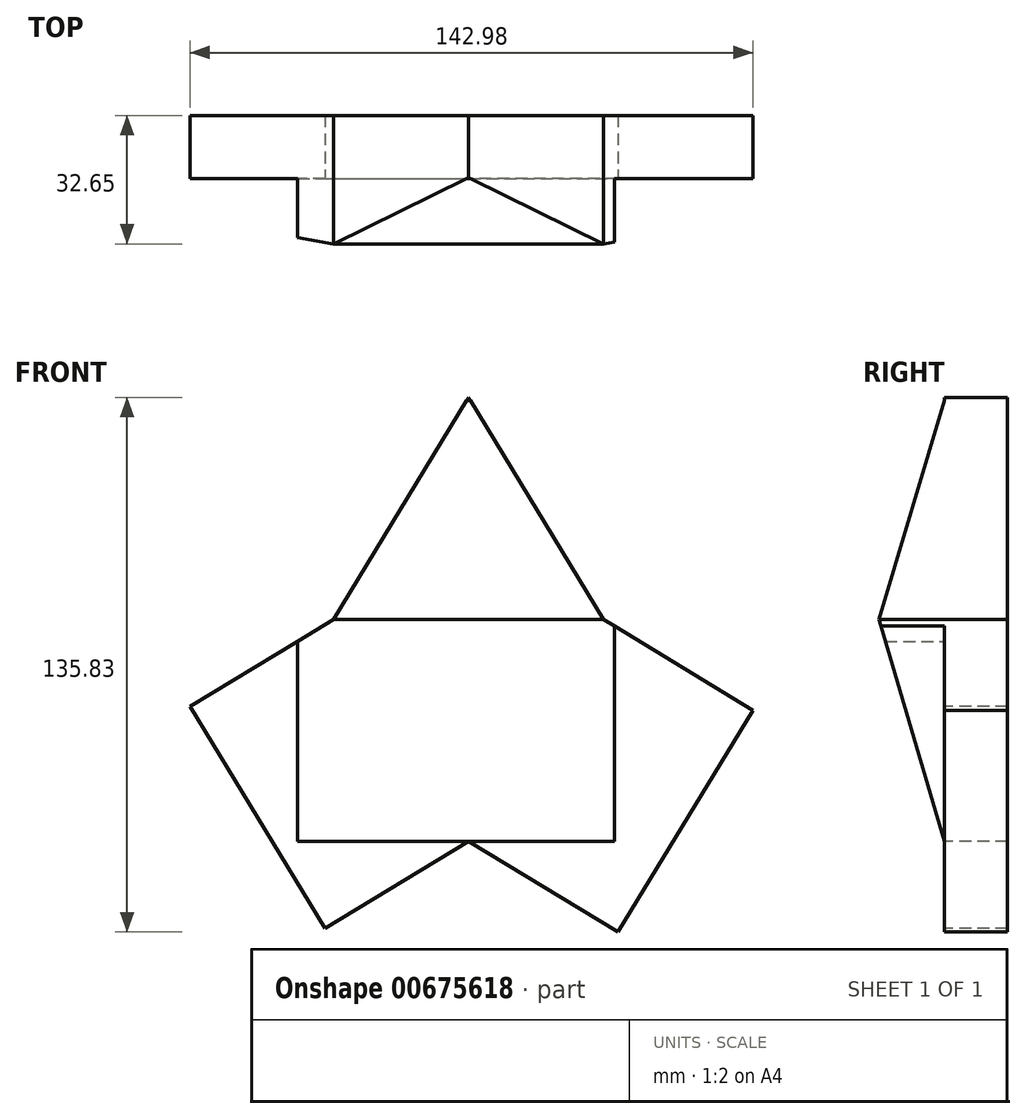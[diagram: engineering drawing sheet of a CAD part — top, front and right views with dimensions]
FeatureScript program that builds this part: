
annotation { "Feature Type Name" : "Feature", "Feature Type Description" : "" }
export const myFeature = defineFeature(function(context is Context, id is Id, definition is map)
    precondition{}
    {
        {
            var Q0;
            Q0=qCreatedBy(makeId("Front.planeOp"),FACE);
            var sketch = newSketch(context, id + "F0", { "sketchPlane" : qUnion([Q0])});
            skLineSegment(sketch, "E0", {"start": v(-34.27, 0) * mm, "end": v(0, 56.37) * mm});
            skLineSegment(sketch, "E1", {"start": v(0, 56.37) * mm, "end": v(34.27, 0) * mm});
            skLineSegment(sketch, "E2", {"start": v(34.27, 0) * mm, "end": v(0, -56.37) * mm});
            skLineSegment(sketch, "E3", {"start": v(0, -56.37) * mm, "end": v(-34.27, 0) * mm});
            skSolve(sketch);
        }
        {
            var Q0;
            Q0=qCreatedBy(makeId("Right.planeOp"),FACE);
            var sketch = newSketch(context, id + "F1", { "sketchPlane" : qUnion([Q0])});
            skLineSegment(sketch, "E4", {"start": v(0, -56.37) * mm, "end": v(-16.65, 0) * mm});
            skLineSegment(sketch, "E5", {"start": v(-16.65, 0) * mm, "end": v(0, 55.53) * mm});
            skLineSegment(sketch, "E6", {"start": v(0, 55.53) * mm, "end": v(0, 0) * mm});
            skLineSegment(sketch, "E7", {"start": v(0, 0) * mm, "end": v(0, -56.37) * mm});
            skSolve(sketch);
        }
        {
            var Q0;
            Q0=makeQuery(id+"F1.imprint","IMPRINT",FACE,{"disambiguationData":[TD([[makeQuery(id+"F1.imprint","IMPRINT",EDGE,{"derivedFrom":sQuery(id+"F1.wireOp",EDGE,"E4")}),-1.0]])]});
            extrude(context, id + "F2", {"entities" : qUnion([Q0]), "oppositeDirection" : true, "depth" : 43.43 * mm, "offsetDistance" : 25.4 * mm});
        }
        {
            var Q0;
            Q0=makeQuery(id+"F2.opExtrude","CAP_FACE",FACE,{"disambiguationData":[OSD([sQuery(id+"F1.wireOp",EDGE,"E4"),sQuery(id+"F1.wireOp",EDGE,"E5"),sQuery(id+"F1.wireOp",EDGE,"E6"),sQuery(id+"F1.wireOp",EDGE,"E7")])],"isStart":true});
            extrude(context, id + "F3", {"entities" : qUnion([Q0]), "operationType" : NewBodyOperationType.ADD, "depth" : 37.08 * mm, "offsetDistance" : 25.4 * mm});
        }
        {
            var Q0;
            Q0=makeQuery(id+"F0.imprint","IMPRINT",FACE,{"disambiguationData":[TD([[makeQuery(id+"F0.imprint","IMPRINT",EDGE,{"derivedFrom":sQuery(id+"F0.wireOp",EDGE,"E0")}),-1.0]])]});
            extrude(context, id + "F4", {"entities" : qUnion([Q0]), "operationType" : NewBodyOperationType.ADD, "oppositeDirection" : true, "depth" : 16 * mm, "offsetDistance" : 25.4 * mm});
        }
        {
            var Q0;
            Q0=makeQuery(id+"F4.opExtrude","SWEPT_FACE",FACE,{"disambiguationData":[OSD([sQuery(id+"F0.wireOp",EDGE,"E3")])]});
            extrude(context, id + "F5", {"entities" : qUnion([Q0]), "operationType" : NewBodyOperationType.ADD, "depth" : 42.67 * mm, "offsetDistance" : 25.4 * mm});
        }
        {
            var Q0;
            Q0=makeQuery(id+"F4.opExtrude","SWEPT_FACE",FACE,{"disambiguationData":[OSD([sQuery(id+"F0.wireOp",EDGE,"E2")])]});
            extrude(context, id + "F6", {"entities" : qUnion([Q0]), "operationType" : NewBodyOperationType.ADD, "depth" : 44.45 * mm, "offsetDistance" : 25.4 * mm});
        }
        {
            var Q0;
            {var subQ0=sQuery(id+"F0.wireOp",EDGE,"E0");var subQ1=sQuery(id+"F1.wireOp",EDGE,"E7");var subQ2=sQuery(id+"F1.wireOp",EDGE,"E6");var subQ3=makeQuery(id+"F2.opExtrude","SWEPT_FACE",FACE,{"disambiguationData":[OSD([subQ2,subQ1])]});var subQ4=makeQuery(id+"F3.opExtrude","SWEPT_FACE",FACE,{"disambiguationData":[OSD([subQ2,subQ1])]});Q0=makeQuery(id+"F4.boolean.opBoolean","SPLIT",FACE,{"disambiguationData":[TD([makeQuery(id+"F4.opExtrude","SWEPT_FACE",FACE,{"disambiguationData":[OSD([subQ0])]})])],"derivedFrom":makeQuery(id+"F3.boolean.opBoolean","MERGE",FACE,{"derivedFrom":[subQ3,subQ4]})});}
            extrude(context, id + "F7", {"entities" : qUnion([Q0]), "operationType" : NewBodyOperationType.REMOVE, "oppositeDirection" : true, "depth" : 25.4 * mm, "offsetDistance" : 25.4 * mm});
        }
        {
            var Q0;
            {var subQ2=sQuery(id+"F0.wireOp",EDGE,"E1");var subQ3=sQuery(id+"F1.wireOp",EDGE,"E7");var subQ4=sQuery(id+"F1.wireOp",EDGE,"E6");var subQ7=makeQuery(id+"F3.opExtrude","SWEPT_FACE",FACE,{"disambiguationData":[OSD([subQ4,subQ3])]});var subQ8=makeQuery(id+"F2.opExtrude","SWEPT_FACE",FACE,{"disambiguationData":[OSD([subQ4,subQ3])]});Q0=makeQuery(id+"F4.boolean.opBoolean","SPLIT",FACE,{"disambiguationData":[TD([makeQuery(id+"F4.opExtrude","SWEPT_FACE",FACE,{"disambiguationData":[OSD([subQ2])]})])],"derivedFrom":makeQuery(id+"F3.boolean.opBoolean","MERGE",FACE,{"derivedFrom":[subQ8,subQ7]})});}
            extrude(context, id + "F8", {"entities" : qUnion([Q0]), "operationType" : NewBodyOperationType.REMOVE, "oppositeDirection" : true, "depth" : 25.4 * mm, "offsetDistance" : 25.4 * mm});
        }
    });
